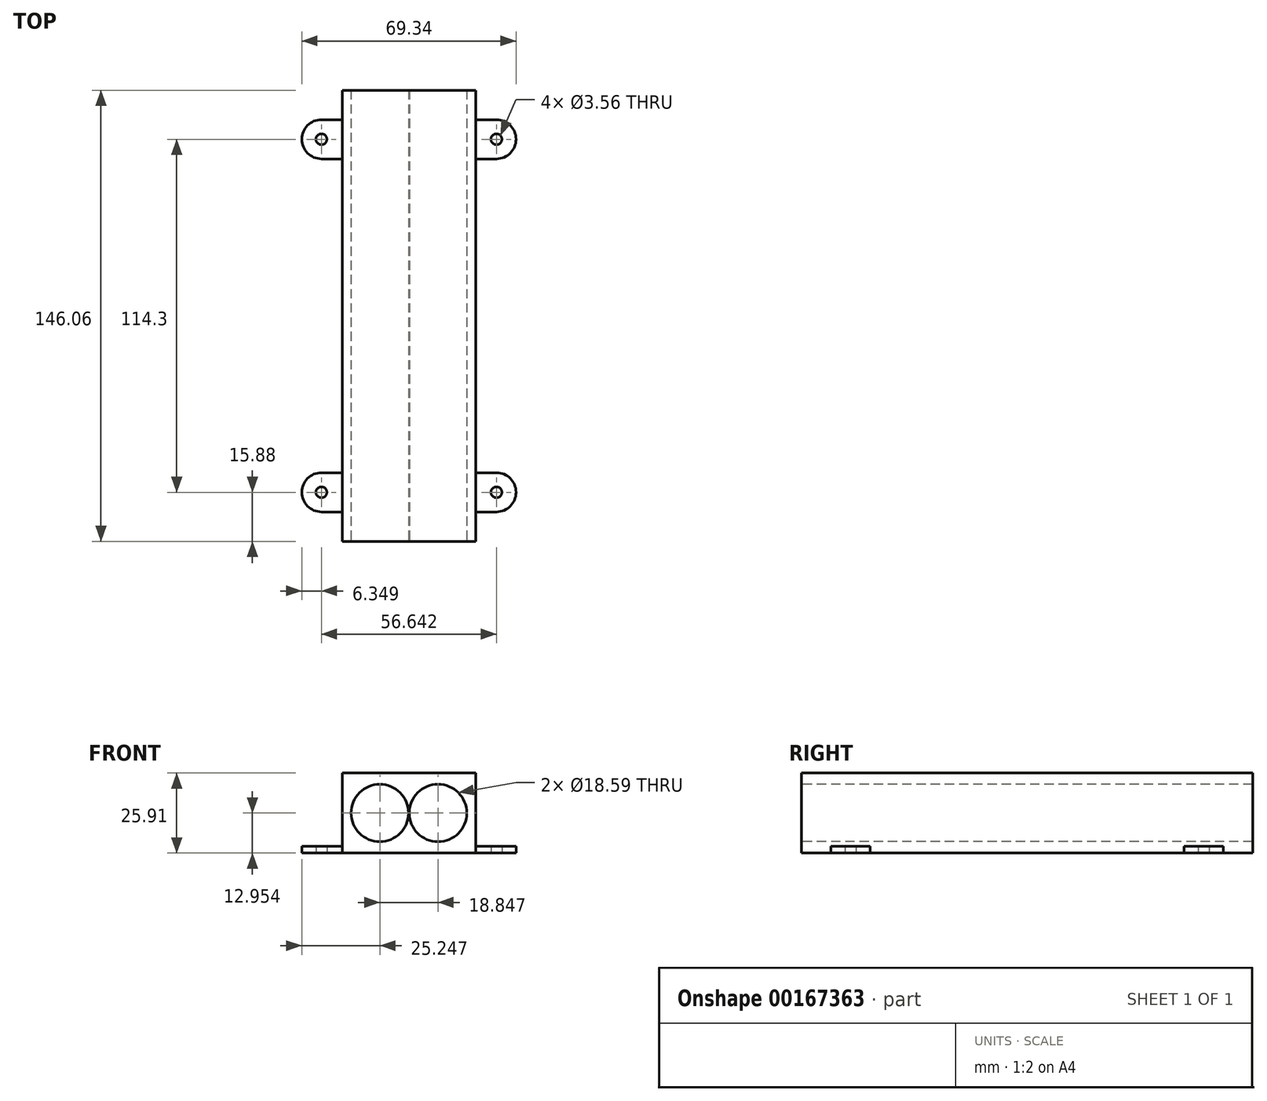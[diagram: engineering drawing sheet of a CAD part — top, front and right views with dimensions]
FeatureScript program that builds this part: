
annotation { "Feature Type Name" : "Feature", "Feature Type Description" : "" }
export const myFeature = defineFeature(function(context is Context, id is Id, definition is map)
    precondition{}
    {
        {
            var Q0;
            Q0=qCreatedBy(makeId("Top.planeOp"),FACE);
            var sketch = newSketch(context, id + "F0", { "sketchPlane" : qUnion([Q0])});
            skLineSegment(sketch, "E0.bottom", {"start": v(21.59, 73.02) * mm, "end": v(-21.59, 73.02) * mm});
            skLineSegment(sketch, "E0.top", {"start": v(21.59, -73.02) * mm, "end": v(-21.59, -73.02) * mm});
            skLineSegment(sketch, "E0.left", {"start": v(21.59, 73.03) * mm, "end": v(21.59, -73.02) * mm});
            skLineSegment(sketch, "E0.right", {"start": v(-21.59, 73.03) * mm, "end": v(-21.59, -73.02) * mm});
            skPoint(sketch, "E0.middle", {"position": v(0, 0) * mm});
            skLineSegment(sketch, "E1.bottom", {"start": v(21.59, 63.5) * mm, "end": v(28.32, 63.5) * mm});
            skLineSegment(sketch, "E1.top", {"start": v(21.59, 50.8) * mm, "end": v(28.32, 50.8) * mm});
            skLineSegment(sketch, "E1.left", {"start": v(21.59, 63.5) * mm, "end": v(21.59, 50.8) * mm});
            skLineSegment(sketch, "E1.right", {"start": v(28.32, 63.5) * mm, "end": v(28.32, 50.8) * mm, "construction": true});
            skArc(sketch, "E2", {"start": v(28.32, 50.8) * mm, "mid": v(34.67, 57.15) * mm, "end": v(28.32, 63.5) * mm});
            skCircle(sketch, "E3", {"center": v(28.32, 57.15) * mm, "radius": 1.78 * mm});
            skLineSegment(sketch, "E4.bottom", {"start": v(21.59, -50.8) * mm, "end": v(28.32, -50.8) * mm});
            skLineSegment(sketch, "E4.top", {"start": v(21.59, -63.5) * mm, "end": v(28.32, -63.5) * mm});
            skLineSegment(sketch, "E4.left", {"start": v(21.59, -50.8) * mm, "end": v(21.59, -63.5) * mm});
            skLineSegment(sketch, "E4.right", {"start": v(28.32, -50.8) * mm, "end": v(28.32, -63.5) * mm, "construction": true});
            skArc(sketch, "E5", {"start": v(28.32, -63.5) * mm, "mid": v(34.67, -57.15) * mm, "end": v(28.32, -50.8) * mm});
            skCircle(sketch, "E6", {"center": v(28.32, -57.15) * mm, "radius": 1.78 * mm});
            skLineSegment(sketch, "E7.bottom", {"start": v(-21.59, 50.8) * mm, "end": v(-28.32, 50.8) * mm});
            skLineSegment(sketch, "E7.top", {"start": v(-21.59, 63.5) * mm, "end": v(-28.32, 63.5) * mm});
            skLineSegment(sketch, "E7.left", {"start": v(-21.59, 50.8) * mm, "end": v(-21.59, 63.5) * mm});
            skLineSegment(sketch, "E7.right", {"start": v(-28.32, 50.8) * mm, "end": v(-28.32, 63.5) * mm, "construction": true});
            skArc(sketch, "E8", {"start": v(-28.32, 63.5) * mm, "mid": v(-34.67, 57.15) * mm, "end": v(-28.32, 50.8) * mm});
            skCircle(sketch, "E9", {"center": v(-28.32, 57.15) * mm, "radius": 1.78 * mm});
            skLineSegment(sketch, "E10.bottom", {"start": v(-21.59, -63.5) * mm, "end": v(-28.32, -63.5) * mm});
            skLineSegment(sketch, "E10.top", {"start": v(-21.59, -50.8) * mm, "end": v(-28.32, -50.8) * mm});
            skLineSegment(sketch, "E10.left", {"start": v(-21.59, -63.5) * mm, "end": v(-21.59, -50.8) * mm});
            skLineSegment(sketch, "E10.right", {"start": v(-28.32, -63.5) * mm, "end": v(-28.32, -50.8) * mm, "construction": true});
            skArc(sketch, "E11", {"start": v(-28.32, -50.8) * mm, "mid": v(-34.67, -57.15) * mm, "end": v(-28.32, -63.5) * mm});
            skCircle(sketch, "E12", {"center": v(-28.32, -57.15) * mm, "radius": 1.78 * mm});
            skLineSegment(sketch, "E13", {"start": v(-21.59, 63.5) * mm, "end": v(21.59, 63.5) * mm, "construction": true});
            skLineSegment(sketch, "E14", {"start": v(-21.59, -50.8) * mm, "end": v(21.59, -50.8) * mm, "construction": true});
            skSolve(sketch);
        }
        {
            var Q0;
            Q0=qSketchRegion(id+"F0",true);
            extrude(context, id + "F1", {"entities" : qUnion([Q0]), "depth" : 2.16 * mm});
        }
        {
            var Q0;
            Q0=makeQuery(id+"F1.opExtrude","CAP_FACE",FACE,{"disambiguationData":[OSD([sQuery(id+"F0.wireOp",EDGE,"E0.bottom"),sQuery(id+"F0.wireOp",EDGE,"E0.top"),sQuery(id+"F0.wireOp",EDGE,"E0.left"),sQuery(id+"F0.wireOp",EDGE,"E0.right"),sQuery(id+"F0.wireOp",EDGE,"E1.bottom"),sQuery(id+"F0.wireOp",EDGE,"E1.top"),sQuery(id+"F0.wireOp",EDGE,"E2"),sQuery(id+"F0.wireOp",EDGE,"E3"),sQuery(id+"F0.wireOp",EDGE,"E4.bottom"),sQuery(id+"F0.wireOp",EDGE,"E4.top"),sQuery(id+"F0.wireOp",EDGE,"E5"),sQuery(id+"F0.wireOp",EDGE,"E6"),sQuery(id+"F0.wireOp",EDGE,"E7.bottom"),sQuery(id+"F0.wireOp",EDGE,"E7.top"),sQuery(id+"F0.wireOp",EDGE,"E8"),sQuery(id+"F0.wireOp",EDGE,"E9"),sQuery(id+"F0.wireOp",EDGE,"E10.bottom"),sQuery(id+"F0.wireOp",EDGE,"E10.top"),sQuery(id+"F0.wireOp",EDGE,"E11"),sQuery(id+"F0.wireOp",EDGE,"E12")])],"isStart":false});
            var sketch = newSketch(context, id + "F2", { "sketchPlane" : qUnion([Q0])});
            skLineSegment(sketch, "E15.bottom", {"start": v(-21.59, 73.02) * mm, "end": v(21.59, 73.02) * mm});
            skLineSegment(sketch, "E15.top", {"start": v(-21.59, -73.02) * mm, "end": v(21.59, -73.02) * mm});
            skLineSegment(sketch, "E15.left", {"start": v(-21.59, 73.02) * mm, "end": v(-21.59, -73.02) * mm});
            skLineSegment(sketch, "E15.right", {"start": v(21.59, 73.02) * mm, "end": v(21.59, -73.02) * mm});
            skSolve(sketch);
        }
        {
            var Q0;
            Q0=qSketchRegion(id+"F2",true);
            extrude(context, id + "F3", {"entities" : qUnion([Q0]), "operationType" : NewBodyOperationType.ADD, "depth" : 21.59 * mm});
        }
        {
            var Q0;
            Q0=makeQuery(id+"F3.opExtrude","CAP_FACE",FACE,{"disambiguationData":[OSD([sQuery(id+"F2.wireOp",EDGE,"E15.bottom"),sQuery(id+"F2.wireOp",EDGE,"E15.top"),sQuery(id+"F2.wireOp",EDGE,"E15.left"),sQuery(id+"F2.wireOp",EDGE,"E15.right")])],"isStart":false});
            var sketch = newSketch(context, id + "F4", { "sketchPlane" : qUnion([Q0])});
            skLineSegment(sketch, "E16.bottom", {"start": v(21.59, 73.02) * mm, "end": v(-21.6, 73.02) * mm});
            skLineSegment(sketch, "E16.top", {"start": v(21.6, -73.02) * mm, "end": v(-21.59, -73.02) * mm});
            skLineSegment(sketch, "E16.left", {"start": v(21.59, 73.02) * mm, "end": v(21.6, -73.02) * mm});
            skLineSegment(sketch, "E16.right", {"start": v(-21.59, 73.02) * mm, "end": v(-21.59, -73.02) * mm});
            skSolve(sketch);
        }
        {
            var Q0;
            Q0=qSketchRegion(id+"F4",true);
            extrude(context, id + "F5", {"entities" : qUnion([Q0]), "operationType" : NewBodyOperationType.ADD, "depth" : 2.16 * mm});
        }
        {
            var Q0;
            Q0=makeQuery(id+"F5.boolean.opBoolean","MERGE",FACE,{"derivedFrom":[makeQuery(id+"F3.boolean.opBoolean","MERGE",FACE,{"derivedFrom":[makeQuery(id+"F1.opExtrude","SWEPT_FACE",FACE,{"disambiguationData":[OSD([sQuery(id+"F0.wireOp",EDGE,"E0.top")])]}),makeQuery(id+"F3.opExtrude","SWEPT_FACE",FACE,{"disambiguationData":[OSD([sQuery(id+"F2.wireOp",EDGE,"E15.top")])]})]}),makeQuery(id+"F5.opExtrude","SWEPT_FACE",FACE,{"disambiguationData":[OSD([sQuery(id+"F4.wireOp",EDGE,"E16.top")])]})]});
            var sketch = newSketch(context, id + "F6", { "sketchPlane" : qUnion([Q0])});
            skCircle(sketch, "E17", {"center": v(-9.42, 12.95) * mm, "radius": 9.3 * mm});
            skLineSegment(sketch, "E18", {"start": v(-21.59, 12.95) * mm, "end": v(21.6, 12.95) * mm, "construction": true});
            skCircle(sketch, "E19", {"center": v(9.42, 12.95) * mm, "radius": 9.3 * mm});
            skLineSegment(sketch, "E20", {"start": v(-21.59, 12.95) * mm, "end": v(-18.72, 12.95) * mm, "construction": true});
            skLineSegment(sketch, "E21", {"start": v(21.6, 12.95) * mm, "end": v(18.72, 12.95) * mm, "construction": true});
            skLineSegment(sketch, "E22.bottom", {"start": v(-0.63, 15.99) * mm, "end": v(0.64, 15.99) * mm});
            skLineSegment(sketch, "E22.top", {"start": v(-0.63, 9.92) * mm, "end": v(0.64, 9.92) * mm});
            skLineSegment(sketch, "E22.left", {"start": v(-0.63, 15.99) * mm, "end": v(-0.63, 9.92) * mm});
            skLineSegment(sketch, "E22.right", {"start": v(0.64, 15.99) * mm, "end": v(0.64, 9.92) * mm});
            skSolve(sketch);
        }
        {
            var Q0;
            {var subQ0=sQuery(id+"F6.wireOp",EDGE,"E22.left");Q0=makeQuery(id+"F6.imprint","IMPRINT",FACE,{"disambiguationData":[TD([[makeQuery(id+"F6.imprint","IMPRINT",EDGE,{"derivedFrom":subQ0}),-1.0]])]});}
            var Q1;
            {var subQ0=sQuery(id+"F6.wireOp",EDGE,"E22.left");Q1=makeQuery(id+"F6.imprint","IMPRINT",FACE,{"disambiguationData":[TD([[makeQuery(id+"F6.imprint","IMPRINT",EDGE,{"derivedFrom":subQ0}),1.0]])]});}
            var Q2;
            {var subQ0=sQuery(id+"F6.wireOp",EDGE,"E22.right");Q2=makeQuery(id+"F6.imprint","IMPRINT",FACE,{"disambiguationData":[TD([[makeQuery(id+"F6.imprint","IMPRINT",EDGE,{"derivedFrom":subQ0}),-1.0]])]});}
            var Q3;
            {var subQ0=sQuery(id+"F6.wireOp",EDGE,"E22.right");Q3=makeQuery(id+"F6.imprint","IMPRINT",FACE,{"disambiguationData":[TD([[makeQuery(id+"F6.imprint","IMPRINT",EDGE,{"derivedFrom":subQ0}),1.0]])]});}
            extrude(context, id + "F7", {"entities" : qUnion([Q0, Q1, Q2, Q3]), "operationType" : NewBodyOperationType.REMOVE, "endBound" : BoundingType.THROUGH_ALL, "oppositeDirection" : true, "depth" : 25.4 * mm});
        }
    });
